# Revit family: Shower-Handshower_Kit-KOHLER-STANCE-K-77989T
name_source: partatom
category: Plumbing Fixtures
revit_build: Autodesk Revit 2017 (Build: 20160225_1515(x64)
units: mm (PartAtom-declared; Revit-internal decimal feet)

## family parameters
Cut with Voids When Loaded = No
Host = Face
OmniClass Number = 23.31.17.00
OmniClass Title = Showers
Part Type = Normal
Room Calculation Point = No
Round Connector Dimension = Use Diameter
Shared = No

## types (6) — shared parameters
ADA Compliant = No
Assembly Code = D2010700
Base = 1 1/16"
CW Connection = Yes
Cold Water Inlet = Cold Water Inlet
Date Modified = 01/18/2021
Default Elevation = 36"
Drain Included = No
Flow Rate = 3 GPM
HW Connection = Yes
Hot Water Inlet = Hot Water Inlet
Manufacturer = KOHLER Co.
Master Format 2014 = 22 42 23
Master Format 2014 Name = Residential Showers
Material = Premium Metal Construction
Pressure = 80.00 psi
Product Documentation Link = https://files.kohler.com.cn
Product Name = STANCE
Product Page URL = https://www.kohler.com.cn
URL = http://www.kohler.com.cn
Vent Connection = No
Waste Connection = No
Waste Water Outlet = Waste Water Outlet
WaterSense Certified = No

## per-type parameters (varying)
| type | 8A | 8AMU | Description | Finish | Height | Length | Model | Type | Width |
| 8A, CP-Polished Chrome | Yes | No | Hand shower with control switch | Kohler-Metal-CP-Polished_Chrome | 9 3/4" | 2 3/8" | K-77989T-8A-CP | 1 | 2 3/8" |
| 8A, TT-Titanium Silver | Yes | No | Hand shower with control switch | Kohler-Metal-TT-Vibrant_Titanium | 9 3/4" | 2 3/8" | K-77989T-8A-TT | 2 | 2 3/8" |
| 8A, 2BL-Primitive Black | Yes | No | Hand shower with control switch | Kohler-Metal-2BL-Original_Black | 9 3/4" | 2 3/8" | K-77989T-8A-2BL | 3 | 2 3/8" |
| 8A,2MB-Vibrant Brushed Moderne Bras | Yes | No | Hand shower with control switch | Kohler-Metal-2MB-Vibrant_Brushed_Moderne_Brass | 9 3/4" | 2 3/8" | -77989T-8A-2MB | 4 | 2 3/8" |
| 8A, 3GC-Black Gold | Yes | No | Hand shower with control switch | Kohler-Metal-3GC-Black_Gold | 9 3/4" | 2 3/8" | K-77989T-8A-3GC | 5 | 2 3/8" |
| 8AMU,BL- Matte black | No | Yes | hand shower with control switch (Manchester United limited edition) | Kohler-Metal-BL-Matte_Black | 9 7/16" | 3 1/8" | K-77989T-8AMU-BL | 6 | 4 15/16" |

## geometry (parser evidence)
native form markers: Sweep x8
no freeform markers — native parametric forms only
